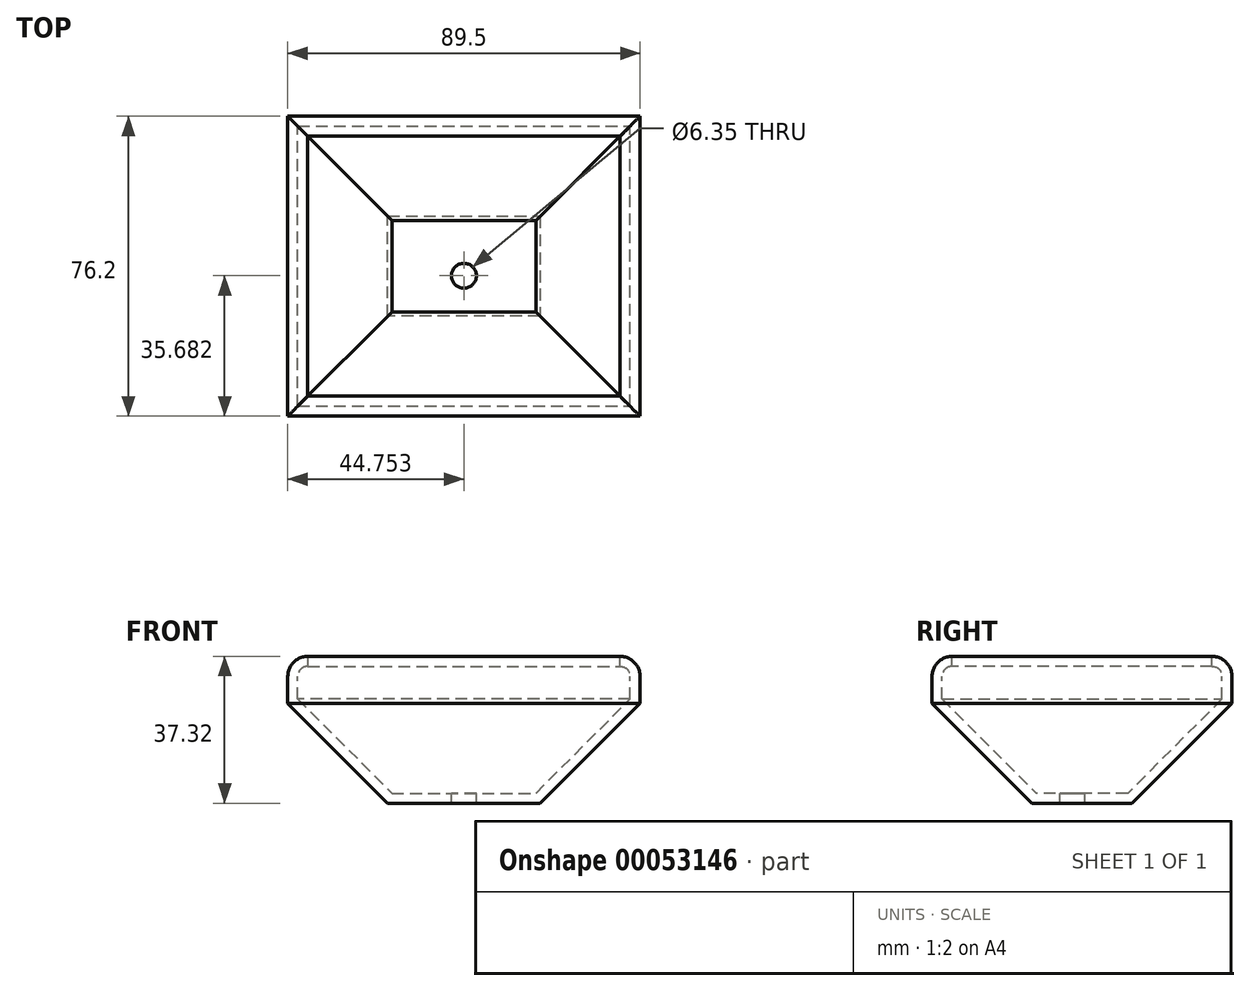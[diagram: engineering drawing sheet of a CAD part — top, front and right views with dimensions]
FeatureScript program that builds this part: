
annotation { "Feature Type Name" : "Feature", "Feature Type Description" : "" }
export const myFeature = defineFeature(function(context is Context, id is Id, definition is map)
    precondition{}
    {
        {
            var Q0;
            Q0=qCreatedBy(makeId("Front.planeOp"),FACE);
            var sketch = newSketch(context, id + "F0", { "sketchPlane" : qUnion([Q0])});
            skLineSegment(sketch, "E0.bottom", {"start": v(44.78, 0) * mm, "end": v(-44.72, 0) * mm});
            skLineSegment(sketch, "E0.top", {"start": v(44.78, 37.32) * mm, "end": v(-44.72, 37.32) * mm});
            skLineSegment(sketch, "E0.left", {"start": v(44.78, 0) * mm, "end": v(44.78, 37.32) * mm});
            skLineSegment(sketch, "E0.right", {"start": v(-44.72, 0) * mm, "end": v(-44.72, 37.32) * mm});
            skSolve(sketch);
        }
        {
            var Q0;
            Q0=makeQuery(id+"F0.imprint","IMPRINT",FACE,{"disambiguationData":[TD([[makeQuery(id+"F0.imprint","IMPRINT",EDGE,{"derivedFrom":sQuery(id+"F0.wireOp",EDGE,"E0.bottom")}),-1.0]])]});
            extrude(context, id + "F1", {"entities" : qUnion([Q0]), "depth" : 76.2 * mm});
        }
        {
            var Q0;
            Q0=makeQuery(id+"F1.opExtrude","SWEPT_EDGE",EDGE,{"disambiguationData":[OSD([sQuery(id+"F0.wireOp",EDGE,"E0.top"),sQuery(id+"F0.wireOp",EDGE,"E0.left")])]});
            var Q1;
            Q1=makeQuery(id+"F1.opExtrude","CAP_EDGE",EDGE,{"disambiguationData":[OSD([sQuery(id+"F0.wireOp",EDGE,"E0.top")])],"isStart":false});
            var Q2;
            Q2=makeQuery(id+"F1.opExtrude","SWEPT_EDGE",EDGE,{"disambiguationData":[OSD([sQuery(id+"F0.wireOp",EDGE,"E0.top"),sQuery(id+"F0.wireOp",EDGE,"E0.right")])]});
            var Q3;
            Q3=makeQuery(id+"F1.opExtrude","CAP_EDGE",EDGE,{"disambiguationData":[OSD([sQuery(id+"F0.wireOp",EDGE,"E0.top")])],"isStart":true});
            fillet(context, id + "F2", {"entities" : qUnion([Q0, Q1, Q2, Q3]), "radius" : 5.08 * mm, "tangentPropagation" : true, "allowEdgeOverflow" : false});
        }
        {
            var Q0;
            Q0=makeQuery(id+"F1.opExtrude","SWEPT_EDGE",EDGE,{"disambiguationData":[OSD([sQuery(id+"F0.wireOp",EDGE,"E0.bottom"),sQuery(id+"F0.wireOp",EDGE,"E0.right")])]});
            var Q1;
            Q1=makeQuery(id+"F1.opExtrude","CAP_EDGE",EDGE,{"disambiguationData":[OSD([sQuery(id+"F0.wireOp",EDGE,"E0.bottom")])],"isStart":true});
            var Q2;
            Q2=makeQuery(id+"F1.opExtrude","SWEPT_EDGE",EDGE,{"disambiguationData":[OSD([sQuery(id+"F0.wireOp",EDGE,"E0.bottom"),sQuery(id+"F0.wireOp",EDGE,"E0.left")])]});
            var Q3;
            Q3=makeQuery(id+"F1.opExtrude","CAP_EDGE",EDGE,{"disambiguationData":[OSD([sQuery(id+"F0.wireOp",EDGE,"E0.bottom")])],"isStart":false});
            chamfer(context, id + "F3", {"entities" : qUnion([Q0, Q1, Q2, Q3]), "width" : 25.4 * mm, "tangentPropagation" : true});
        }
        {
            var Q0;
            Q0=makeQuery(id+"F1.opExtrude","SWEPT_FACE",FACE,{"disambiguationData":[OSD([sQuery(id+"F0.wireOp",EDGE,"E0.top")])]});
            shell(context, id + "F4", {"entities" : qUnion([Q0]), "thickness" : 2.54 * mm});
        }
        {
            var Q0;
            {var subQ0=sQuery(id+"F0.wireOp",EDGE,"E0.bottom");Q0=makeQuery(id+"F4.opShell","OFFSET_FACE",FACE,{"disambiguationData":[OSD([subQ0]),TDD([makeQuery(id+"F1.opExtrude","SWEPT_FACE",FACE,{"disambiguationData":[OSD([subQ0])]})])]});}
            var sketch = newSketch(context, id + "F5", { "sketchPlane" : qUnion([Q0])});
            skPoint(sketch, "E1", {"position": v(0.03, -40.52) * mm});
            skPoint(sketch, "E1.positionSnap0", {"position": v(0.03, -49.75) * mm});
            skSolve(sketch);
        }
        {
            var Q0;
            Q0=sQuery(id+"F5.wireOp",VERTEX,"E1");
            var Q1;
            Q1=makeQuery(id+"F1.opExtrude","SWEPT_BODY",BODY,{"disambiguationData":[OSD([sQuery(id+"F0.wireOp",EDGE,"E0.bottom"),sQuery(id+"F0.wireOp",EDGE,"E0.top"),sQuery(id+"F0.wireOp",EDGE,"E0.left"),sQuery(id+"F0.wireOp",EDGE,"E0.right")])]});
            hole(context, id + "F6", {"style" : HoleStyle.SIMPLE, "holeDiameter" : 6.35 * mm, "endStyle" : HoleEndStyle.THROUGH, "locations" : qUnion([Q0]), "scope" : qUnion([Q1])});
        }
    });
